# Revit family: FU_Chair_Sandler_OSWELL 1-1
name_source: partatom
category: Furniture
units: mm (PartAtom-declared; Revit-internal decimal feet)

## family parameters
Always vertical = Yes
Cut with Voids When Loaded = No
OmniClass Number = 23.40.20.00
OmniClass Title = General Furniture and Specialties
Render Appearance Source = Family Geometry
Room Calculation Point = No
Shared = No
Work Plane-Based = No

## types (1)
- Oswell 1.1
    Default Elevation = 0 mm  [stored 0 ft]
    Depth = 540 mm  [stored 1.77165 ft]
    Description = Stackable side chair with seat pad. This sled-based chair stacks up to 40 units high on the OSW0122OP trolley. Greenguard Gold-certified to protect indoor air quality.
    Height = 815 mm  [stored 2.67388 ft]
    Manufacturer = Sandler
    Model = Oswell 1.1
    URL = https://www.sandlerseating.com
    Width = 515 mm  [stored 1.68963 ft]

note: [stored X ft] marks values corroborated as IEEE doubles in the binary element streams (Revit-internal decimal feet)

## geometry (parser evidence)
native form markers: Sweep x9
no freeform markers — native parametric forms only
